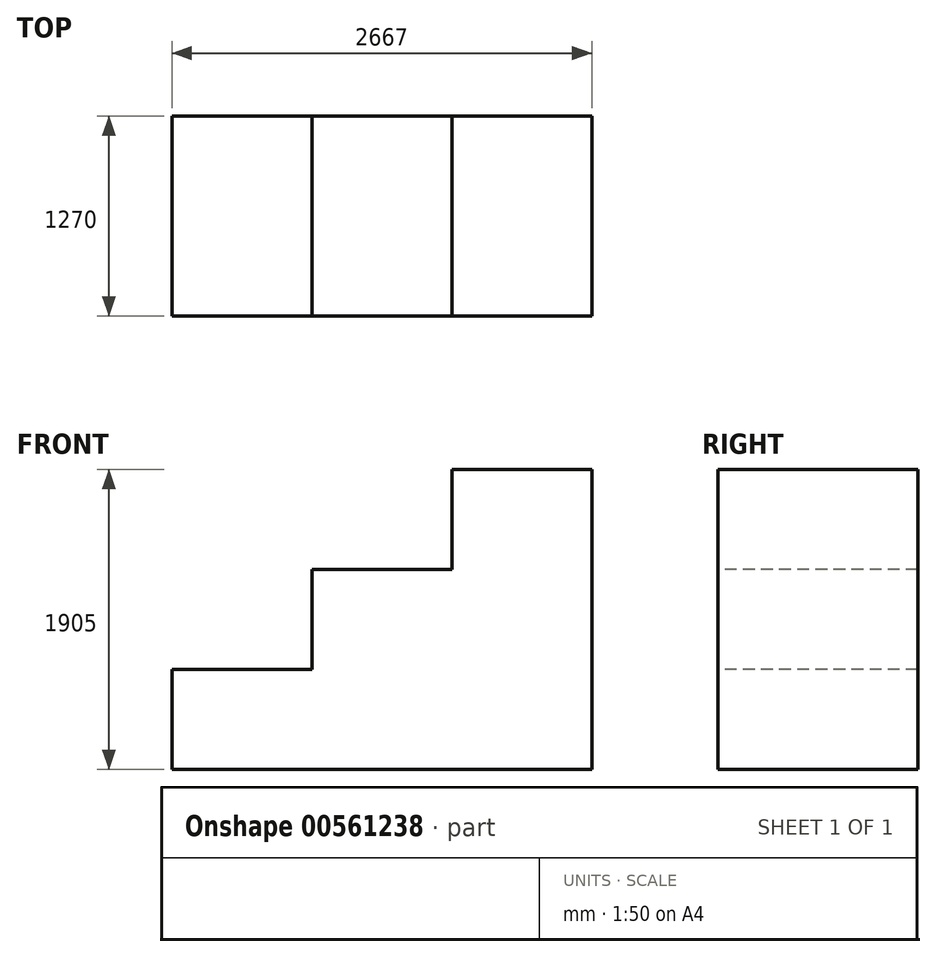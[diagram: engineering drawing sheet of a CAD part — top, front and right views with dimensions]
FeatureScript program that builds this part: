
annotation { "Feature Type Name" : "Feature", "Feature Type Description" : "" }
export const myFeature = defineFeature(function(context is Context, id is Id, definition is map)
    precondition{}
    {
        {
            var Q0;
            Q0=qCreatedBy(makeId("Front.planeOp"),FACE);
            var sketch = newSketch(context, id + "F0", { "sketchPlane" : qUnion([Q0])});
            skLineSegment(sketch, "E0.bottom", {"start": v(1714.39, 952.61) * mm, "end": v(-952.61, 952.61) * mm});
            skLineSegment(sketch, "E0.top", {"start": v(1714.39, -952.39) * mm, "end": v(-952.61, -952.39) * mm});
            skLineSegment(sketch, "E0.left", {"start": v(1714.39, 952.61) * mm, "end": v(1714.39, -952.39) * mm});
            skLineSegment(sketch, "E0.right", {"start": v(-952.61, 952.61) * mm, "end": v(-952.61, -952.39) * mm});
            skSolve(sketch);
        }
        {
            var Q0;
            Q0 = qSketchRegion(id + "F0", true);
            extrude(context, id + "F1", {"entities" : qUnion([Q0]), "depth" : 1270 * mm, "offsetDistance" : 25.4 * mm});
        }
        {
            var Q0;
            Q0=makeQuery(id+"F1.opExtrude","CAP_FACE",FACE,{"disambiguationData":[OSD([sQuery(id+"F0.wireOp",EDGE,"E0.bottom"),sQuery(id+"F0.wireOp",EDGE,"E0.top"),sQuery(id+"F0.wireOp",EDGE,"E0.left"),sQuery(id+"F0.wireOp",EDGE,"E0.right")])],"isStart":false});
            var sketch = newSketch(context, id + "F2", { "sketchPlane" : qUnion([Q0])});
            skLineSegment(sketch, "E1", {"start": v(-952.61, -952.39) * mm, "end": v(-952.61, -317.39) * mm});
            skLineSegment(sketch, "E2", {"start": v(-952.61, -317.39) * mm, "end": v(-63.61, -317.39) * mm});
            skLineSegment(sketch, "E3", {"start": v(-63.61, -317.39) * mm, "end": v(-63.61, 317.61) * mm});
            skLineSegment(sketch, "E4", {"start": v(-63.61, 317.61) * mm, "end": v(825.39, 317.61) * mm});
            skLineSegment(sketch, "E5", {"start": v(825.39, 317.61) * mm, "end": v(825.39, 952.61) * mm});
            skSolve(sketch);
        }
        {
            var Q0;
            {var subQ1=sQuery(id+"F2.wireOp",EDGE,"E2");Q0=makeQuery(id+"F2.imprint","IMPRINT",FACE,{"disambiguationData":[TD([[makeQuery(id+"F2.imprint","IMPRINT",EDGE,{"derivedFrom":subQ1}),1.0]])]});}
            extrude(context, id + "F3", {"entities" : qUnion([Q0]), "operationType" : NewBodyOperationType.REMOVE, "endBound" : BoundingType.THROUGH_ALL, "oppositeDirection" : true, "depth" : 25.4 * mm, "offsetDistance" : 25.4 * mm});
        }
    });
